# Revit family: Diverter_Trim-American_Standard-Aspirations-TU061740_Series
name_source: partatom
category: Plumbing Fixtures
units: mm (PartAtom-declared; Revit-internal decimal feet)

## family parameters
Cut with Voids When Loaded = No
Host = Face
OmniClass Number = 23.65.55.14
OmniClass Title = Valves for Liquid Services
Part Type = Normal
Room Calculation Point = No
Round Connector Dimension = Use Diameter
Shared = Yes

## types (3) — shared parameters
3rd Outlet Water Connection Diameter = 0"
ADA Compliant = Yes
CW Connection = Yes
CWFU = 3
Compliance Certifications = These products meet or exceed the following codes and standards: ASSE 1016, ASME A112.18.1, CSA B125.1
Default Elevation = 40"
Description = Flash™ 2-Handle Integrated Diverter Pressure Balance Valve Trim
Diameter = 7 7/8"
Distance From Wall = 2"
HW Connection = Yes
HWFU = 3
Height = 7 7/8"
Installation Type = Wall Mounted
Manufacturer = American Standard
RU520 Flash Rough Valve Body = Yes
Rough Valve Visibility = Yes
URL = https://www.americanstandard-us.com
Vent Connection = No
WFU = 4
Waste Connection = No
Water Connection Diameter = 1/2"

## per-type parameters (varying)
| type | Assembly Code | Finish | Material |
| TU061740.002 | D2010710 | Brass-American Standard-002-Polished Chrome | Brass-American Standard-002-Polished Chrome |
| TU061740.295 | D2020 | Brass-American Standard-295-Satin Nickel | Brass-American Standard-295-Satin Nickel |
| TU061740.243 | D2020 | Brass-American Standard-243-Matte Black | Brass-American Standard-243-Matte Black |

note: column(s) folded — value = type name in every type: Model

## geometry (parser evidence)
native form markers: Sweep x2
no freeform markers — native parametric forms only
